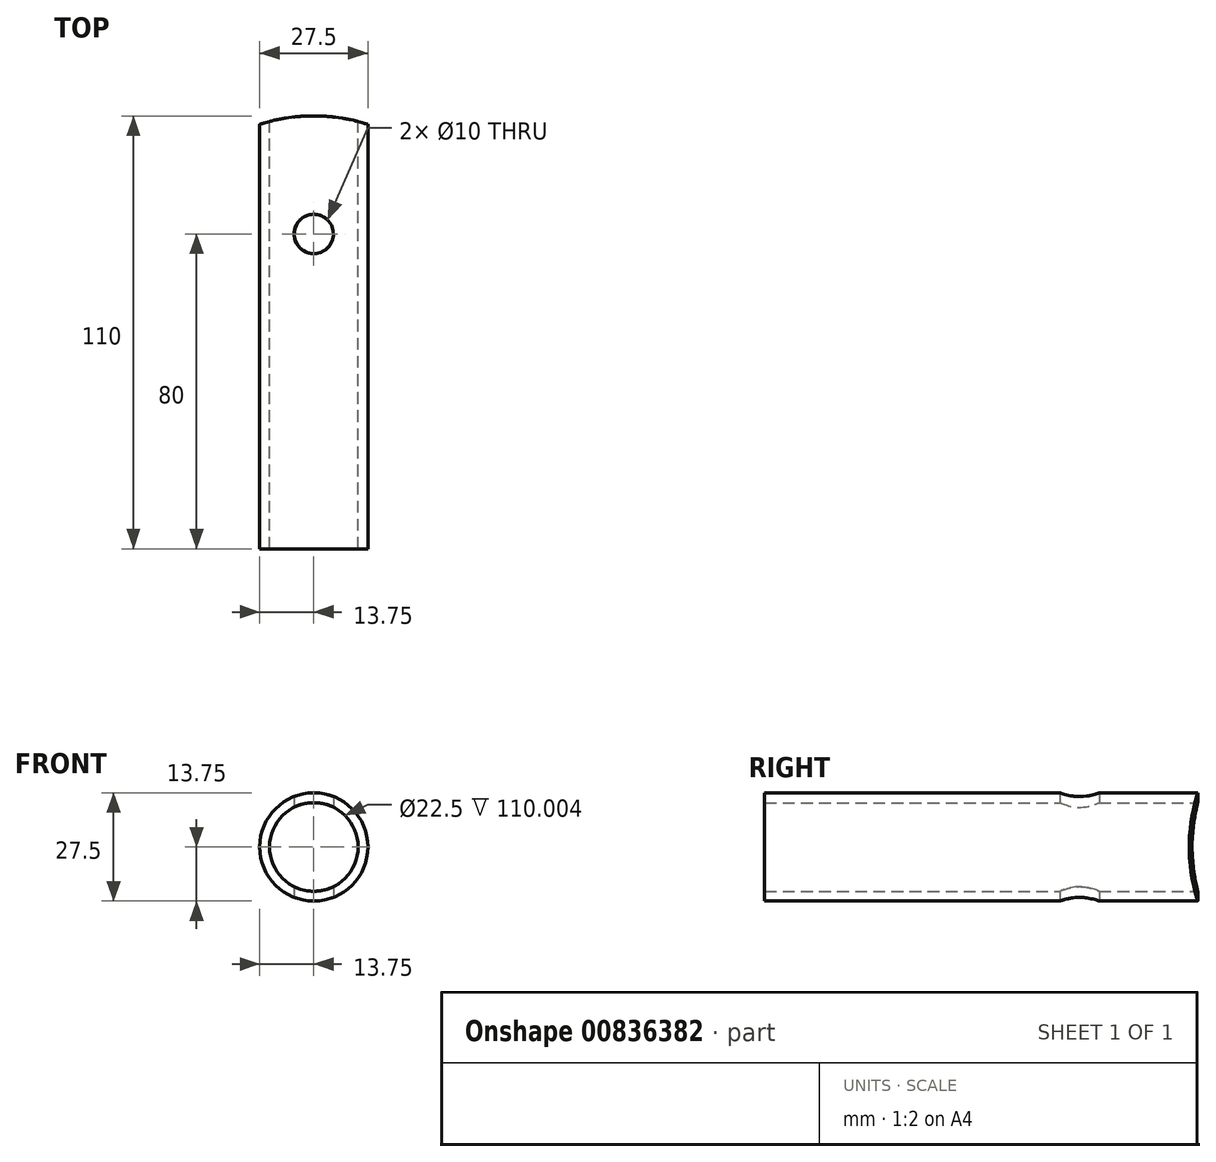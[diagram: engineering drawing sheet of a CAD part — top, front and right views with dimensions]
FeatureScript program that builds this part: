
annotation { "Feature Type Name" : "Feature", "Feature Type Description" : "" }
export const myFeature = defineFeature(function(context is Context, id is Id, definition is map)
    precondition{}
    {
        {
            var Q0;
            Q0=qCreatedBy(makeId("Front.planeOp"),FACE);
            var sketch = newSketch(context, id + "F0", { "sketchPlane" : qUnion([Q0])});
            skCircle(sketch, "E0", {"center": v(0, 0) * mm, "radius": 13.75 * mm});
            skCircle(sketch, "E1", {"center": v(0, 0) * mm, "radius": 11.25 * mm});
            skSolve(sketch);
        }
        {
            var Q0;
            Q0=makeQuery(id+"F0.imprint","IMPRINT",FACE,{"disambiguationData":[TD([[makeQuery(id+"F0.imprint","IMPRINT",EDGE,{"derivedFrom":sQuery(id+"F0.wireOp",EDGE,"E0")}),1.0]])]});
            extrude(context, id + "F1", {"entities" : qUnion([Q0]), "depth" : 110 * mm, "offsetDistance" : 25 * mm});
        }
        {
            var Q0;
            Q0=qCreatedBy(makeId("Top.planeOp"),FACE);
            var sketch = newSketch(context, id + "F2", { "sketchPlane" : qUnion([Q0])});
            skCircle(sketch, "E2", {"center": v(0, -25) * mm, "radius": 5 * mm});
            skLineSegment(sketch, "E3", {"start": v(0, 0) * mm, "end": v(0, -57.6) * mm, "construction": true});
            skLineSegment(sketch, "E4", {"start": v(0, -25) * mm, "end": v(-40.42, -25) * mm, "construction": true});
            skLineSegment(sketch, "E5", {"start": v(-40.42, -25) * mm, "end": v(30.62, -25) * mm, "construction": true});
            skSolve(sketch);
        }
        {
            var Q0;
            Q0=qCreatedBy(makeId("Top.planeOp"),FACE);
            cPlane(context, id + "F3", {"entities" : qUnion([Q0]), "cplaneType" : CPlaneType.OFFSET, "offset" : 20 * mm, "oppositeDirection" : true, "width" : 150 * mm, "height" : 150 * mm});
        }
        {
            var Q0;
            Q0=qCreatedBy(id+"F3.planeOp",FACE);
            var sketch = newSketch(context, id + "F4", { "sketchPlane" : qUnion([Q0])});
            skCircle(sketch, "E6", {"center": v(0, -30) * mm, "radius": 5 * mm});
            skLineSegment(sketch, "E7", {"start": v(-21.24, -2.52) * mm, "end": v(-21.24, 7.67) * mm});
            skLineSegment(sketch, "E8", {"start": v(-21.24, 7.67) * mm, "end": v(21.4, 6.8) * mm});
            skLineSegment(sketch, "E9", {"start": v(21.4, 6.8) * mm, "end": v(21.4, -2.56) * mm});
            skLineSegment(sketch, "E10", {"start": v(0, 0) * mm, "end": v(0, -45) * mm, "construction": true});
            skArc(sketch, "E11", {"start": v(21.4, -5.41) * mm, "mid": v(0.09, 0) * mm, "end": v(-21.24, -5.33) * mm});
            skPoint(sketch, "E12.center.orphan", {"position": v(0, -90.88) * mm});
            skLineSegment(sketch, "E13", {"start": v(-21.24, -2.52) * mm, "end": v(-21.24, -6.87) * mm});
            skLineSegment(sketch, "E14", {"start": v(21.4, -2.56) * mm, "end": v(21.4, -5.41) * mm});
            skSolve(sketch);
        }
        {
            var Q0;
            Q0=makeQuery(id+"F4.imprint","IMPRINT",FACE,{"disambiguationData":[TD([[makeQuery(id+"F4.imprint","IMPRINT",EDGE,{"derivedFrom":sQuery(id+"F4.wireOp",EDGE,"E6")}),1.0]])]});
            extrude(context, id + "F5", {"entities" : qUnion([Q0]), "operationType" : NewBodyOperationType.REMOVE, "endBound" : BoundingType.THROUGH_ALL, "depth" : 25 * mm, "offsetDistance" : 25 * mm});
        }
        {
            var Q0;
            Q0=makeQuery(id+"F4.imprint","IMPRINT",FACE,{"disambiguationData":[TD([[makeQuery(id+"F4.imprint","IMPRINT",EDGE,{"derivedFrom":sQuery(id+"F4.wireOp",EDGE,"E7")}),-1.0]])]});
            extrude(context, id + "F6", {"entities" : qUnion([Q0]), "operationType" : NewBodyOperationType.REMOVE, "endBound" : BoundingType.THROUGH_ALL, "depth" : 25 * mm, "offsetDistance" : 25 * mm});
        }
    });
